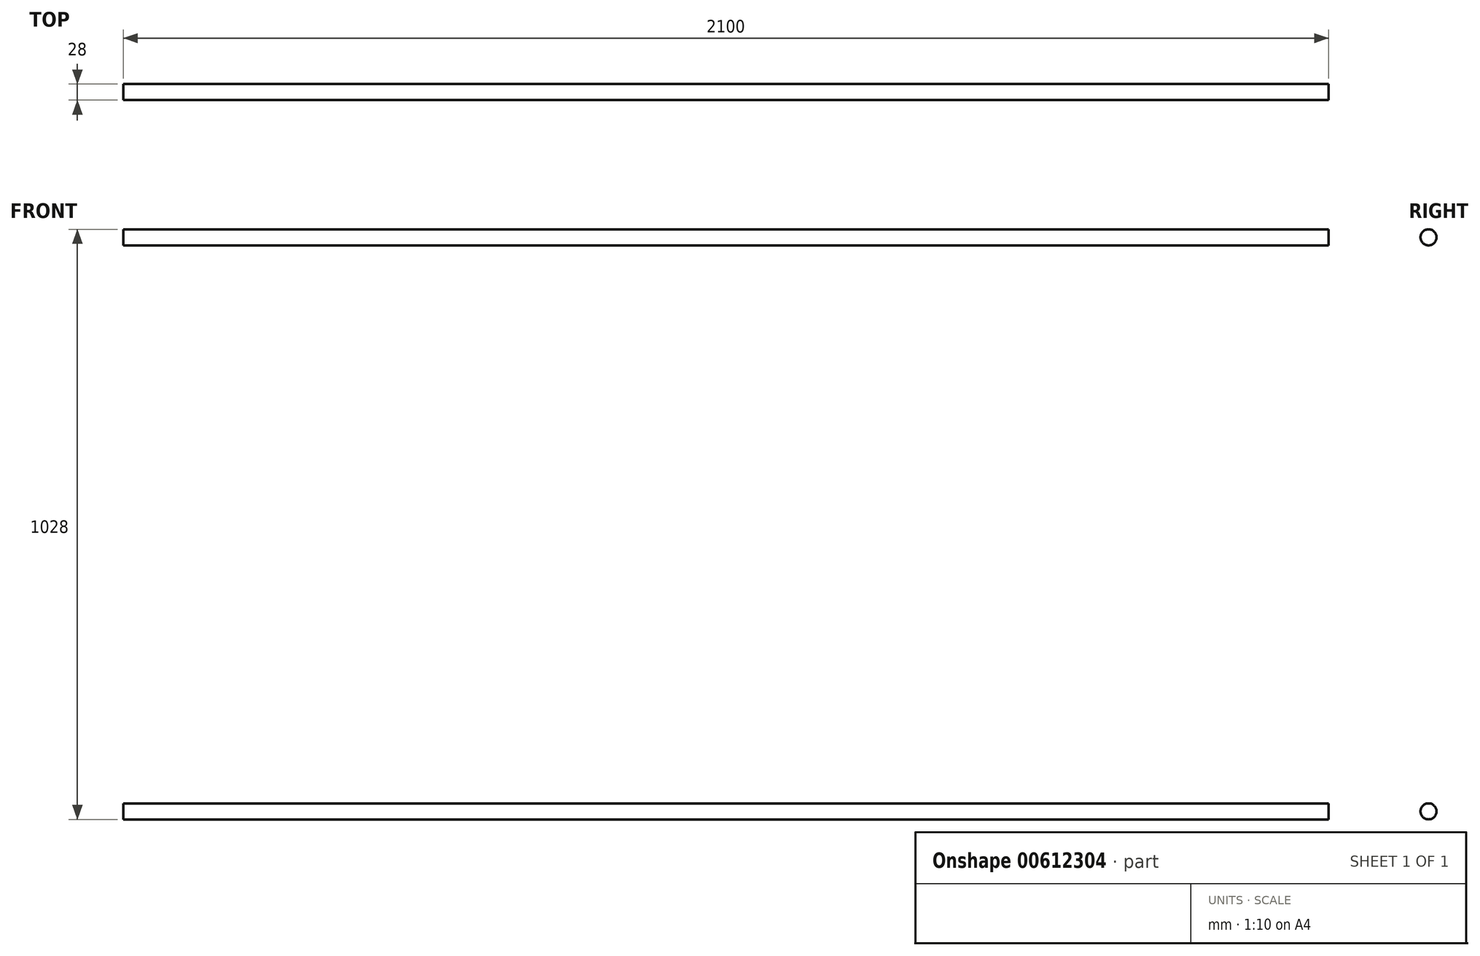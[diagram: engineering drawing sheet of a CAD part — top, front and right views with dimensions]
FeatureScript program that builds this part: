
annotation { "Feature Type Name" : "Feature", "Feature Type Description" : "" }
export const myFeature = defineFeature(function(context is Context, id is Id, definition is map)
    precondition{}
    {
        {
            var Q0;
            Q0=qCreatedBy(makeId("Right.planeOp"),FACE);
            var sketch = newSketch(context, id + "F0", { "sketchPlane" : qUnion([Q0])});
            skCircle(sketch, "E0", {"center": v(0, 0) * mm, "radius": 14 * mm});
            skSolve(sketch);
        }
        {
            var Q0;
            Q0=makeQuery(id+"F0.imprint","IMPRINT",FACE,{"disambiguationData":[TD([[makeQuery(id+"F0.imprint","IMPRINT",EDGE,{"derivedFrom":sQuery(id+"F0.wireOp",EDGE,"E0")}),1.0]])]});
            extrude(context, id + "F1", {"entities" : qUnion([Q0]), "depth" : 2100 * mm, "offsetDistance" : 25 * mm});
        }
        {
            var Q0;
            Q0=makeQuery(id+"F1.opExtrude","SWEPT_BODY",BODY,{"disambiguationData":[OSD([sQuery(id+"F0.wireOp",EDGE,"E0")])]});
            transform(context, id + "F2", {"entities" : qUnion([Q0]), "transformType" : TransformType.TRANSLATION_3D, "dx" : 0 * mm, "dy" : 0 * mm, "dz" : 1000 * mm, "makeCopy" : true});
        }
    });
